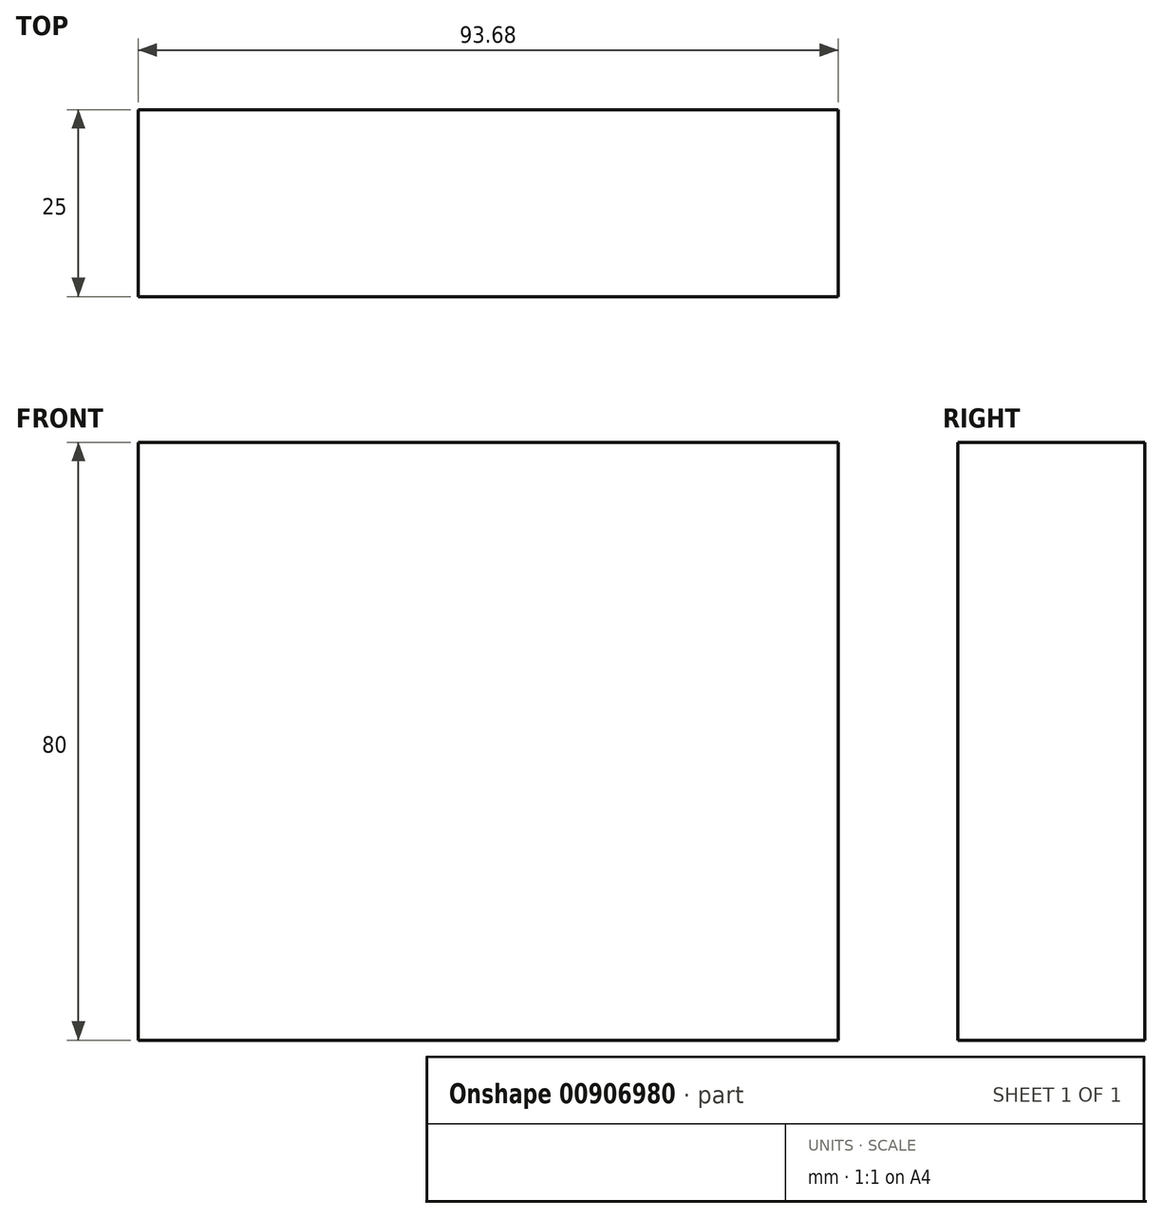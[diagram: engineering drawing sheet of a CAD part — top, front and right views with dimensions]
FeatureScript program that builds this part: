
annotation { "Feature Type Name" : "Feature", "Feature Type Description" : "" }
export const myFeature = defineFeature(function(context is Context, id is Id, definition is map)
    precondition{}
    {
        {
            var Q0;
            Q0=qCreatedBy(makeId("Front.planeOp"),FACE);
            var sketch = newSketch(context, id + "F0", { "sketchPlane" : qUnion([Q0])});
            skLineSegment(sketch, "E0.bottom", {"start": v(46.84, -40) * mm, "end": v(-46.84, -40) * mm});
            skLineSegment(sketch, "E0.top", {"start": v(46.84, 40) * mm, "end": v(-46.84, 40) * mm});
            skLineSegment(sketch, "E0.left", {"start": v(46.84, -40) * mm, "end": v(46.84, 40) * mm});
            skLineSegment(sketch, "E0.right", {"start": v(-46.84, -40) * mm, "end": v(-46.84, 40) * mm});
            skPoint(sketch, "E0.middle", {"position": v(0, 0) * mm});
            skSolve(sketch);
        }
        {
            var Q0;
            Q0=makeQuery(id+"F0.imprint","IMPRINT",FACE,{"disambiguationData":[TD([[makeQuery(id+"F0.imprint","IMPRINT",EDGE,{"derivedFrom":sQuery(id+"F0.wireOp",EDGE,"E0.bottom")}),-1.0]])]});
            extrude(context, id + "F1", {"entities" : qUnion([Q0]), "depth" : 25 * mm, "offsetDistance" : 25 * mm});
        }
    });
